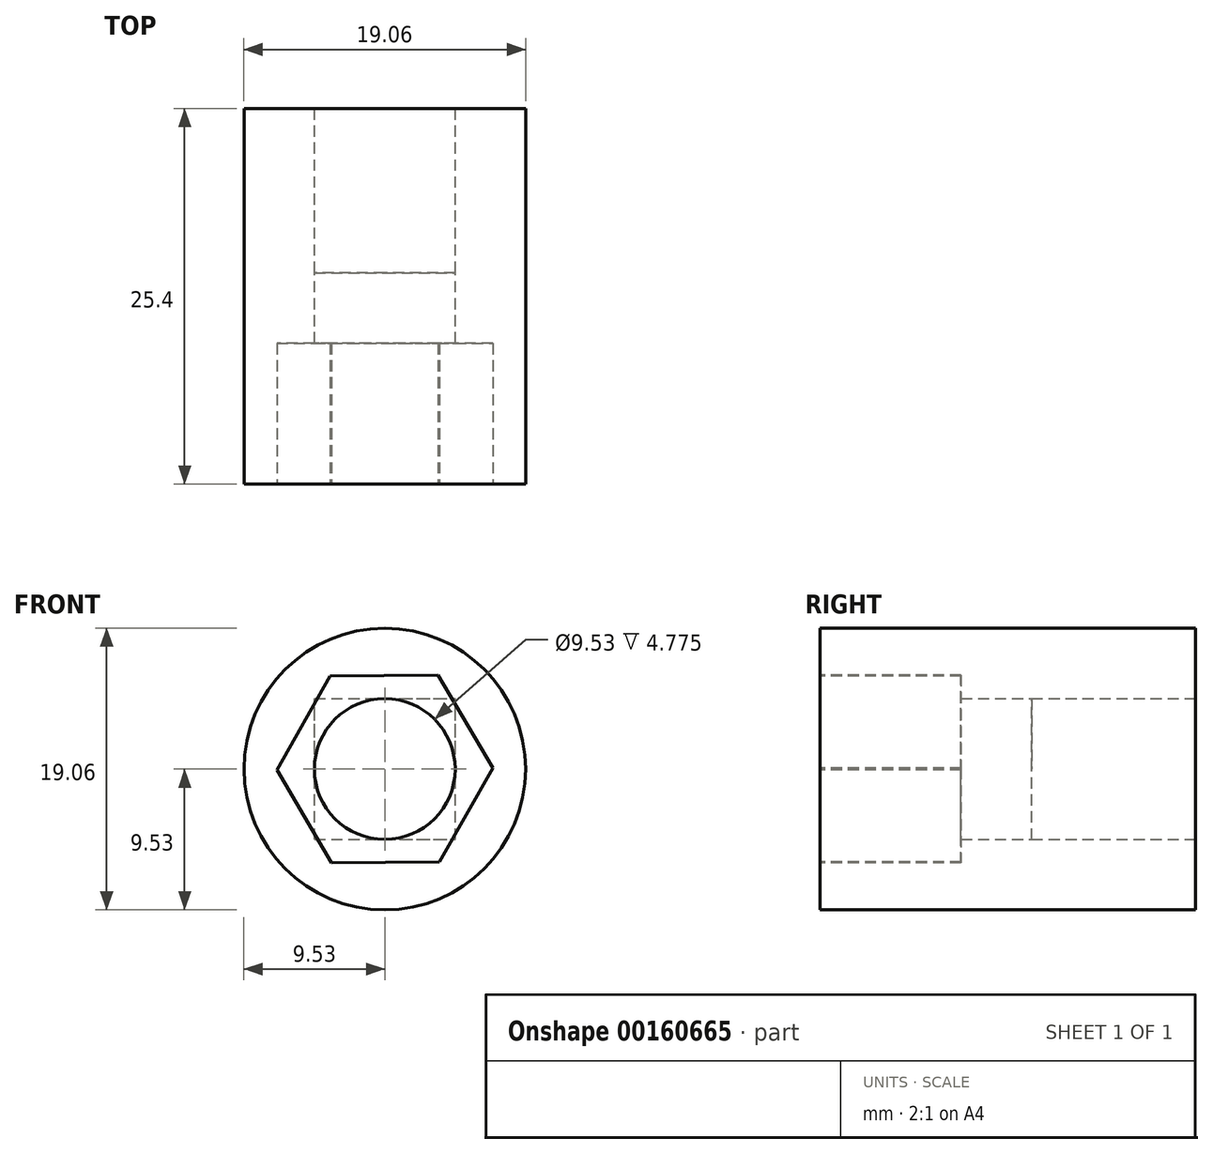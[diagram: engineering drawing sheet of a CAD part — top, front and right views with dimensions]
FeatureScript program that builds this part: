
annotation { "Feature Type Name" : "Feature", "Feature Type Description" : "" }
export const myFeature = defineFeature(function(context is Context, id is Id, definition is map)
    precondition{}
    {
        {
            var Q0;
            Q0=qCreatedBy(makeId("Front.planeOp"),FACE);
            var sketch = newSketch(context, id + "F0", { "sketchPlane" : qUnion([Q0])});
            skCircle(sketch, "E0", {"center": v(0, 0) * mm, "radius": 9.53 * mm});
            skSolve(sketch);
        }
        {
            var Q0;
            Q0=makeQuery(id+"F0.imprint","IMPRINT",FACE,{"disambiguationData":[TD([[makeQuery(id+"F0.imprint","IMPRINT",EDGE,{"derivedFrom":sQuery(id+"F0.wireOp",EDGE,"E0")}),1.0]])]});
            extrude(context, id + "F1", {"entities" : qUnion([Q0]), "oppositeDirection" : true, "depth" : 25.4 * mm});
        }
        {
            var Q0;
            Q0=makeQuery(id+"F1.opExtrude","CAP_FACE",FACE,{"disambiguationData":[OSD([sQuery(id+"F0.wireOp",EDGE,"E0")])],"isStart":false});
            var sketch = newSketch(context, id + "F2", { "sketchPlane" : qUnion([Q0])});
            skLineSegment(sketch, "E1.bottom", {"start": v(4.76, -4.76) * mm, "end": v(-4.76, -4.76) * mm});
            skLineSegment(sketch, "E1.top", {"start": v(4.76, 4.76) * mm, "end": v(-4.76, 4.76) * mm});
            skLineSegment(sketch, "E1.left", {"start": v(4.76, -4.76) * mm, "end": v(4.76, 4.76) * mm});
            skLineSegment(sketch, "E1.right", {"start": v(-4.76, -4.76) * mm, "end": v(-4.76, 4.76) * mm});
            skPoint(sketch, "E1.middle", {"position": v(0, 0) * mm});
            skCircle(sketch, "E2", {"center": v(0, 0) * mm, "radius": 4.76 * mm});
            skSolve(sketch);
        }
        {
            var Q0;
            {var subQ0=sQuery(id+"F2.wireOp",EDGE,"E2");var subQ1=makeQuery(id+"F2.imprint","INTERSECT",VERTEX,{"derivedFrom":[sQuery(id+"F2.wireOp",EDGE,"E1.top"),subQ0]});Q0=makeQuery(id+"F2.imprint","IMPRINT",FACE,{"disambiguationData":[TD([[makeQuery(id+"F2.imprint","IMPRINT",EDGE,{"disambiguationData":[TD([[subQ1,1.0]])],"derivedFrom":subQ0}),1.0]])]});}
            var Q1;
            Q1=sQuery(id+"F2.wireOp",EDGE,"E2");
            extrude(context, id + "F3", {"entities" : qUnion([Q0]), "operationType" : NewBodyOperationType.REMOVE, "surfaceEntities" : qUnion([Q1]), "endBound" : BoundingType.THROUGH_ALL, "oppositeDirection" : true, "depth" : 25.4 * mm});
        }
        {
            var Q0;
            Q0 = qSketchRegion(id + "F2", true);
            extrude(context, id + "F4", {"entities" : qUnion([Q0]), "operationType" : NewBodyOperationType.REMOVE, "oppositeDirection" : true, "depth" : 11.1 * mm});
        }
        {
            var Q0;
            Q0=makeQuery(id+"F1.opExtrude","CAP_FACE",FACE,{"disambiguationData":[OSD([sQuery(id+"F0.wireOp",EDGE,"E0")])],"isStart":true});
            var sketch = newSketch(context, id + "F5", { "sketchPlane" : qUnion([Q0])});
            skCircle(sketch, "E3.cCircle", {"center": v(0, 0) * mm, "radius": 6.32 * mm, "construction": true});
            skLineSegment(sketch, "E3.0", {"start": v(7.3, 0.06) * mm, "end": v(3.7, -6.3) * mm});
            skLineSegment(sketch, "E3.1", {"start": v(3.7, -6.3) * mm, "end": v(-3.6, -6.36) * mm});
            skLineSegment(sketch, "E3.2", {"start": v(-3.6, -6.36) * mm, "end": v(-7.3, -0.06) * mm});
            skLineSegment(sketch, "E3.3", {"start": v(-7.3, -0.06) * mm, "end": v(-3.7, 6.3) * mm});
            skLineSegment(sketch, "E3.4", {"start": v(-3.7, 6.3) * mm, "end": v(3.6, 6.36) * mm});
            skLineSegment(sketch, "E3.5", {"start": v(3.6, 6.36) * mm, "end": v(7.3, 0.06) * mm});
            skPoint(sketch, "E3.0.midPoint", {"position": v(5.5, -3.12) * mm});
            skSolve(sketch);
        }
        {
            var Q0;
            Q0 = qSketchRegion(id + "F5", true);
            extrude(context, id + "F6", {"entities" : qUnion([Q0]), "operationType" : NewBodyOperationType.REMOVE, "oppositeDirection" : true, "depth" : 9.52 * mm});
        }
    });
